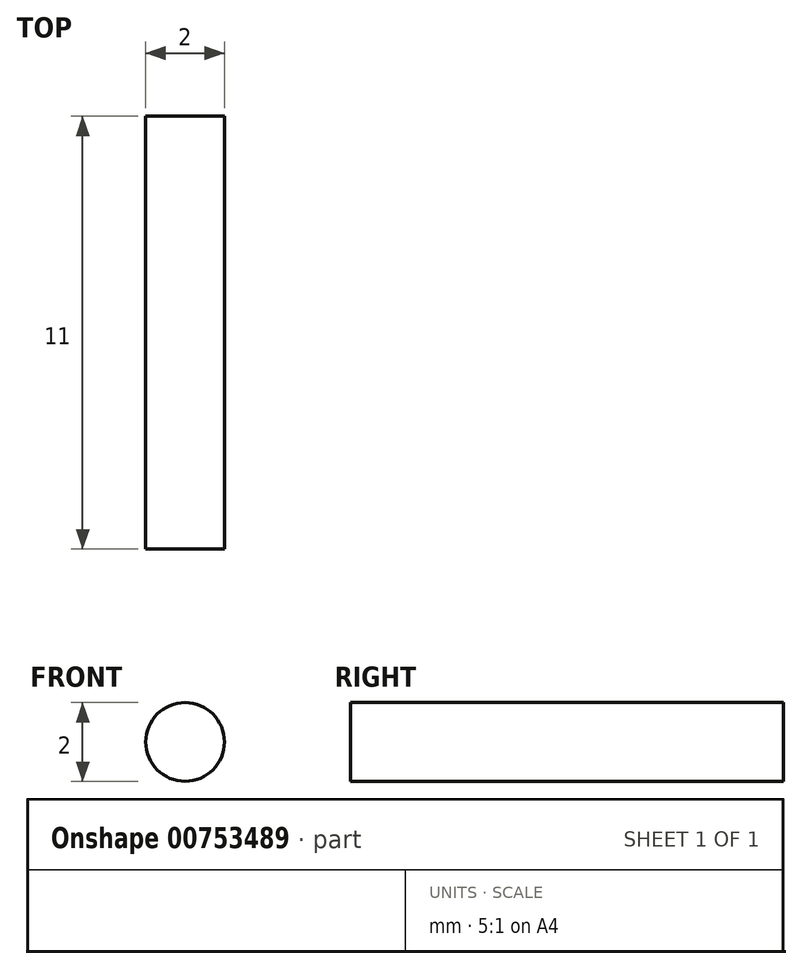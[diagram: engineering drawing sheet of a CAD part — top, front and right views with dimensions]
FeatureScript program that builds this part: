
annotation { "Feature Type Name" : "Feature", "Feature Type Description" : "" }
export const myFeature = defineFeature(function(context is Context, id is Id, definition is map)
    precondition{}
    {
        {
            var Q0;
            Q0=qCreatedBy(makeId("Front.planeOp"),FACE);
            var sketch = newSketch(context, id + "F0", { "sketchPlane" : qUnion([Q0])});
            skCircle(sketch, "E0", {"center": v(0, 0) * mm, "radius": 1 * mm});
            skSolve(sketch);
        }
        {
            var Q0;
            Q0=makeQuery(id+"F0.imprint","IMPRINT",FACE,{"disambiguationData":[TD([[makeQuery(id+"F0.imprint","IMPRINT",EDGE,{"derivedFrom":sQuery(id+"F0.wireOp",EDGE,"E0")}),1.0]])]});
            extrude(context, id + "F1", {"entities" : qUnion([Q0]), "depth" : 11 * mm, "offsetDistance" : 25.4 * mm});
        }
    });
